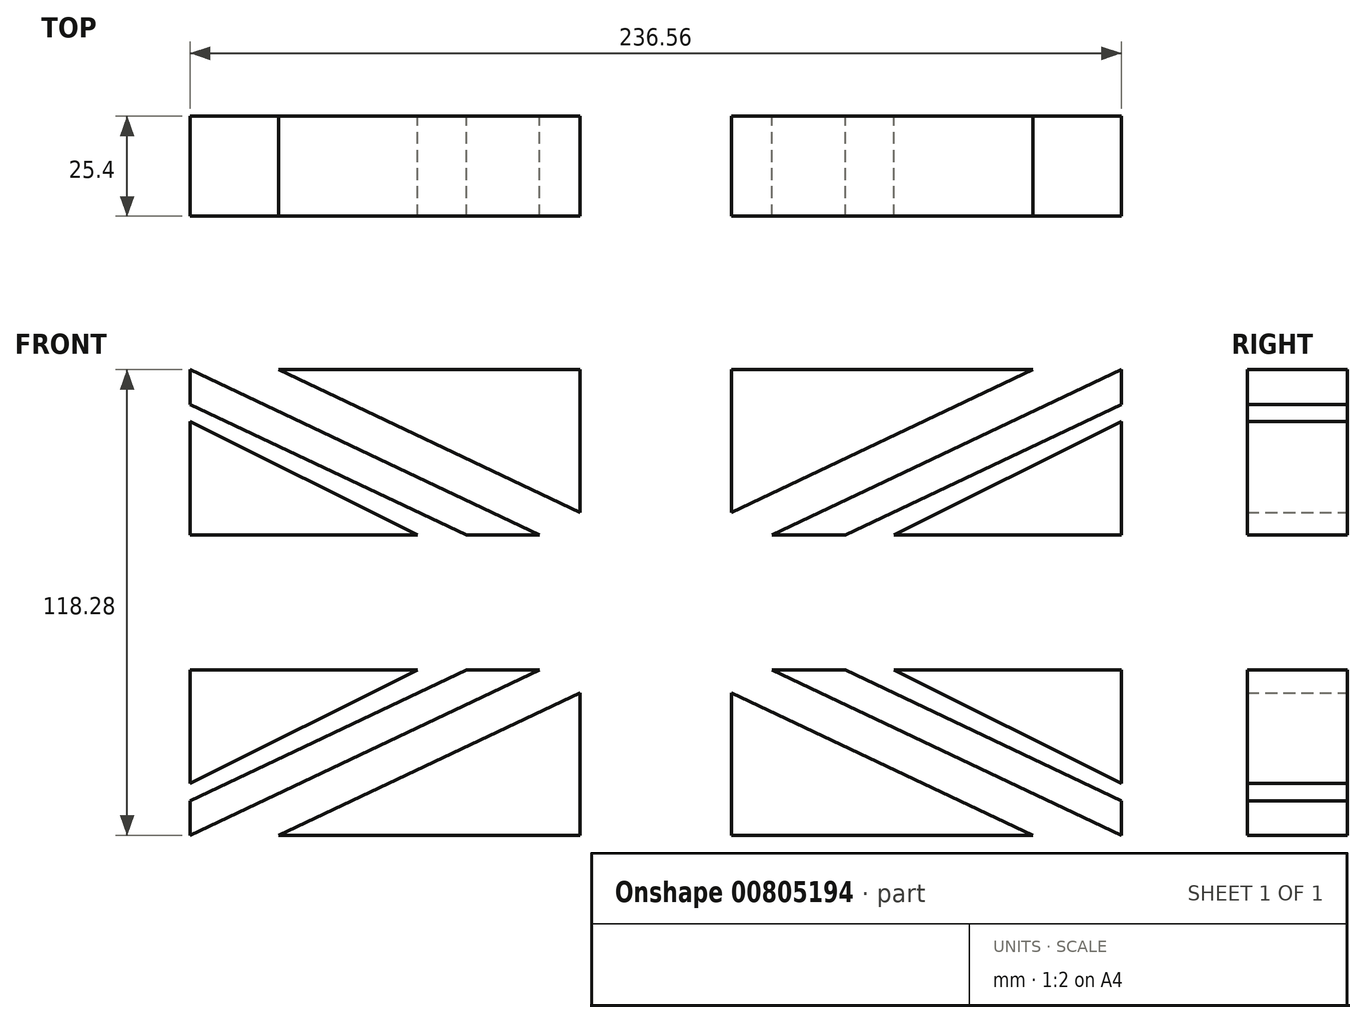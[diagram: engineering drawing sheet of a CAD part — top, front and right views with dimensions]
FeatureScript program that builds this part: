
annotation { "Feature Type Name" : "Feature", "Feature Type Description" : "" }
export const myFeature = defineFeature(function(context is Context, id is Id, definition is map)
    precondition{}
    {
        {
            var Q0;
            Q0=qCreatedBy(makeId("Front.planeOp"),FACE);
            var sketch = newSketch(context, id + "F0", { "sketchPlane" : qUnion([Q0])});
            skLineSegment(sketch, "E0", {"start": v(-125.14, 56.42) * mm, "end": v(-67.32, 27.62) * mm});
            skLineSegment(sketch, "E1", {"start": v(-67.32, 27.62) * mm, "end": v(-125.14, 27.62) * mm});
            skLineSegment(sketch, "E2", {"start": v(-125.14, 27.62) * mm, "end": v(-125.14, 56.42) * mm});
            skLineSegment(sketch, "E3", {"start": v(-125.14, 69.6) * mm, "end": v(-36.39, 27.62) * mm});
            skLineSegment(sketch, "E4", {"start": v(-36.39, 27.62) * mm, "end": v(-54.99, 27.62) * mm});
            skLineSegment(sketch, "E5", {"start": v(-54.99, 27.62) * mm, "end": v(-125.14, 60.8) * mm});
            skLineSegment(sketch, "E6", {"start": v(-125.14, 60.8) * mm, "end": v(-125.14, 69.6) * mm});
            skLineSegment(sketch, "E7", {"start": v(-26.11, 69.6) * mm, "end": v(-26.11, 33.37) * mm});
            skLineSegment(sketch, "E8", {"start": v(-26.11, 33.37) * mm, "end": v(-102.7, 69.6) * mm});
            skLineSegment(sketch, "E9", {"start": v(-102.7, 69.6) * mm, "end": v(-26.11, 69.6) * mm});
            skLineSegment(sketch, "E10", {"start": v(-6.86, 69.6) * mm, "end": v(-6.86, -48.68) * mm, "construction": true});
            skLineSegment(sketch, "E11", {"start": v(-125.14, 10.46) * mm, "end": v(111.42, 10.46) * mm, "construction": true});
            skLineSegment(sketch, "E12.MirrorCS", {"start": v(12.4, 69.6) * mm, "end": v(12.4, 33.37) * mm});
            skLineSegment(sketch, "E13.MirrorCS", {"start": v(12.4, 33.37) * mm, "end": v(88.98, 69.6) * mm});
            skLineSegment(sketch, "E14.MirrorCS", {"start": v(88.98, 69.6) * mm, "end": v(12.4, 69.6) * mm});
            skLineSegment(sketch, "E15.MirrorCS", {"start": v(22.68, 27.62) * mm, "end": v(41.27, 27.62) * mm});
            skLineSegment(sketch, "E16.MirrorCS", {"start": v(111.42, 69.6) * mm, "end": v(22.68, 27.62) * mm});
            skLineSegment(sketch, "E17.MirrorCS", {"start": v(41.27, 27.62) * mm, "end": v(111.42, 60.8) * mm});
            skLineSegment(sketch, "E18.MirrorCS", {"start": v(111.42, 60.8) * mm, "end": v(111.42, 69.6) * mm});
            skLineSegment(sketch, "E19.MirrorCS", {"start": v(111.42, 56.42) * mm, "end": v(53.6, 27.62) * mm});
            skLineSegment(sketch, "E20.MirrorCS", {"start": v(53.6, 27.62) * mm, "end": v(111.42, 27.62) * mm});
            skLineSegment(sketch, "E21.MirrorCS", {"start": v(111.42, 27.62) * mm, "end": v(111.42, 56.42) * mm});
            skLineSegment(sketch, "E22.MirrorCS", {"start": v(-67.32, -6.7) * mm, "end": v(-125.14, -6.7) * mm});
            skLineSegment(sketch, "E23.MirrorCS", {"start": v(-125.14, -35.5) * mm, "end": v(-67.32, -6.7) * mm});
            skLineSegment(sketch, "E24.MirrorCS", {"start": v(-125.14, -6.7) * mm, "end": v(-125.14, -35.5) * mm});
            skLineSegment(sketch, "E25.MirrorCS", {"start": v(-125.14, -39.89) * mm, "end": v(-125.14, -48.68) * mm});
            skLineSegment(sketch, "E26.MirrorCS", {"start": v(-54.99, -6.7) * mm, "end": v(-125.14, -39.89) * mm});
            skLineSegment(sketch, "E27.MirrorCS", {"start": v(-125.14, -48.68) * mm, "end": v(-36.39, -6.7) * mm});
            skLineSegment(sketch, "E28.MirrorCS", {"start": v(-36.39, -6.7) * mm, "end": v(-54.99, -6.7) * mm});
            skLineSegment(sketch, "E29.MirrorCS", {"start": v(-26.11, -12.46) * mm, "end": v(-102.7, -48.68) * mm});
            skLineSegment(sketch, "E30.MirrorCS", {"start": v(-26.11, -48.68) * mm, "end": v(-26.11, -12.46) * mm});
            skLineSegment(sketch, "E31.MirrorCS", {"start": v(-102.7, -48.68) * mm, "end": v(-26.11, -48.68) * mm});
            skLineSegment(sketch, "E32.MirrorCS", {"start": v(12.4, -48.68) * mm, "end": v(12.4, -12.46) * mm});
            skLineSegment(sketch, "E33.MirrorCS", {"start": v(88.98, -48.68) * mm, "end": v(12.4, -48.68) * mm});
            skLineSegment(sketch, "E34.MirrorCS", {"start": v(12.4, -12.46) * mm, "end": v(88.98, -48.68) * mm});
            skLineSegment(sketch, "E35.MirrorCS", {"start": v(111.42, -48.68) * mm, "end": v(22.68, -6.7) * mm});
            skLineSegment(sketch, "E36.MirrorCS", {"start": v(41.27, -6.7) * mm, "end": v(111.42, -39.89) * mm});
            skLineSegment(sketch, "E37.MirrorCS", {"start": v(22.68, -6.7) * mm, "end": v(41.27, -6.7) * mm});
            skLineSegment(sketch, "E38.MirrorCS", {"start": v(111.42, -39.89) * mm, "end": v(111.42, -48.68) * mm});
            skLineSegment(sketch, "E39.MirrorCS", {"start": v(111.42, -6.7) * mm, "end": v(111.42, -35.5) * mm});
            skLineSegment(sketch, "E40.MirrorCS", {"start": v(111.42, -35.5) * mm, "end": v(53.6, -6.7) * mm});
            skLineSegment(sketch, "E41.MirrorCS", {"start": v(53.6, -6.7) * mm, "end": v(111.42, -6.7) * mm});
            skSolve(sketch);
        }
        {
            var Q0;
            Q0=makeQuery(id+"F0.imprint","IMPRINT",FACE,{"disambiguationData":[TD([[makeQuery(id+"F0.imprint","IMPRINT",EDGE,{"derivedFrom":sQuery(id+"F0.wireOp",EDGE,"E3")}),-1.0]])]});
            var Q1;
            Q1=makeQuery(id+"F0.imprint","IMPRINT",FACE,{"disambiguationData":[TD([[makeQuery(id+"F0.imprint","IMPRINT",EDGE,{"derivedFrom":sQuery(id+"F0.wireOp",EDGE,"E7")}),-1.0]])]});
            var Q2;
            Q2=makeQuery(id+"F0.imprint","IMPRINT",FACE,{"disambiguationData":[TD([[makeQuery(id+"F0.imprint","IMPRINT",EDGE,{"derivedFrom":sQuery(id+"F0.wireOp",EDGE,"E0")}),-1.0]])]});
            var Q3;
            Q3=makeQuery(id+"F0.imprint","IMPRINT",FACE,{"disambiguationData":[TD([[makeQuery(id+"F0.imprint","IMPRINT",EDGE,{"derivedFrom":sQuery(id+"F0.wireOp",EDGE,"E12.MirrorCS")}),1.0]])]});
            var Q4;
            Q4=makeQuery(id+"F0.imprint","IMPRINT",FACE,{"disambiguationData":[TD([[makeQuery(id+"F0.imprint","IMPRINT",EDGE,{"derivedFrom":sQuery(id+"F0.wireOp",EDGE,"E15.MirrorCS")}),1.0]])]});
            var Q5;
            Q5=makeQuery(id+"F0.imprint","IMPRINT",FACE,{"disambiguationData":[TD([[makeQuery(id+"F0.imprint","IMPRINT",EDGE,{"derivedFrom":sQuery(id+"F0.wireOp",EDGE,"E19.MirrorCS")}),1.0]])]});
            var Q6;
            Q6=makeQuery(id+"F0.imprint","IMPRINT",FACE,{"disambiguationData":[TD([[makeQuery(id+"F0.imprint","IMPRINT",EDGE,{"derivedFrom":sQuery(id+"F0.wireOp",EDGE,"E39.MirrorCS")}),-1.0]])]});
            var Q7;
            Q7=makeQuery(id+"F0.imprint","IMPRINT",FACE,{"disambiguationData":[TD([[makeQuery(id+"F0.imprint","IMPRINT",EDGE,{"derivedFrom":sQuery(id+"F0.wireOp",EDGE,"E35.MirrorCS")}),-1.0]])]});
            var Q8;
            Q8=makeQuery(id+"F0.imprint","IMPRINT",FACE,{"disambiguationData":[TD([[makeQuery(id+"F0.imprint","IMPRINT",EDGE,{"derivedFrom":sQuery(id+"F0.wireOp",EDGE,"E32.MirrorCS")}),-1.0]])]});
            var Q9;
            Q9=makeQuery(id+"F0.imprint","IMPRINT",FACE,{"disambiguationData":[TD([[makeQuery(id+"F0.imprint","IMPRINT",EDGE,{"derivedFrom":sQuery(id+"F0.wireOp",EDGE,"E29.MirrorCS")}),1.0]])]});
            var Q10;
            Q10=makeQuery(id+"F0.imprint","IMPRINT",FACE,{"disambiguationData":[TD([[makeQuery(id+"F0.imprint","IMPRINT",EDGE,{"derivedFrom":sQuery(id+"F0.wireOp",EDGE,"E25.MirrorCS")}),1.0]])]});
            var Q11;
            Q11=makeQuery(id+"F0.imprint","IMPRINT",FACE,{"disambiguationData":[TD([[makeQuery(id+"F0.imprint","IMPRINT",EDGE,{"derivedFrom":sQuery(id+"F0.wireOp",EDGE,"E22.MirrorCS")}),1.0]])]});
            extrude(context, id + "F1", {"entities" : qUnion([Q0, Q1, Q2, Q3, Q4, Q5, Q6, Q7, Q8, Q9, Q10, Q11]), "depth" : 25.4 * mm, "offsetDistance" : 25.4 * mm});
        }
    });
